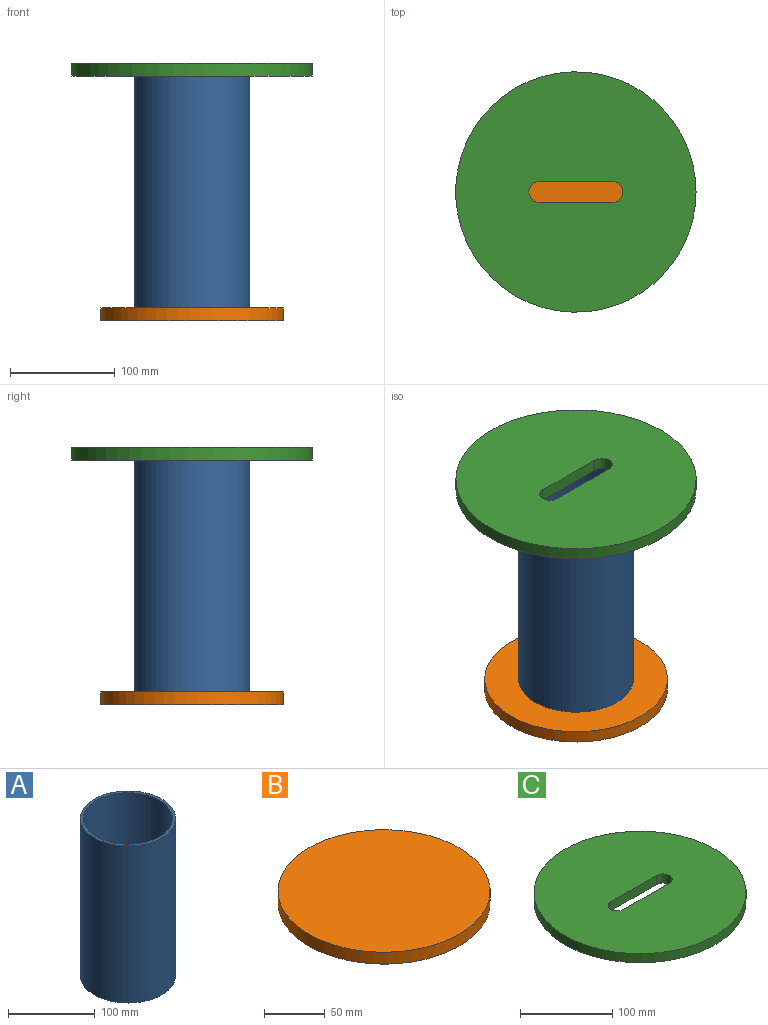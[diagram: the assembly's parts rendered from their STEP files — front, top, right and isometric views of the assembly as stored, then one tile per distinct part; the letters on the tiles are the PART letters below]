
ASSEMBLY  parts=3 mates=3
PART A: 4 faces, bbox 110x110x222 mm
  f0: cylinder r=51.5mm len=222mm, axis (0,0,-1), area 71835.7mm2, adj f2,f3
  f1: cylinder r=55mm len=222mm, axis (0,0,-1), area 76717.7mm2, adj f2,f3
  f2: plane 110x110mm, normal (0,0,1), area 1171mm2, adj f0,f1
  f3: plane 110x110mm, normal (0,0,-1), area 1171mm2, adj f0,f1
PART B: 3 faces, bbox 175x175x12 mm
  f0: cylinder r=87.5mm len=175mm, axis (0,0,-1), area 6597.3mm2, adj f1,f2
  f1: plane 175x175mm, normal (0,0,1), area 24052.8mm2, adj f0
  f2: plane 175x175mm, normal (0,0,-1), area 24052.8mm2, adj f0
PART C: 7 faces, bbox 230x230x12 mm
  f0: cylinder r=115mm len=230mm, axis (0,0,-1), area 8670.8mm2, adj f1,f2
  f1: plane 230x230mm, normal (0,0,1), area 39833.4mm2, adj f0,f3,f4,f5,f6
  f2: plane 230x230mm, normal (0,0,-1), area 39833.4mm2, adj f0,f3,f4,f5,f6
  f3: plane 70x12mm, normal (0,-1,0), area 840mm2, adj f1,f2,f4,f6
  f4: cylinder r=10mm len=20mm, axis (0,0,1), area 377mm2, adj f1,f2,f3,f5
  f5: plane 70x12mm, normal (0,1,0), area 840mm2, adj f1,f2,f4,f6
  f6: cylinder r=10mm len=20mm, axis (0,0,1), area 377mm2, adj f1,f2,f3,f5
PLACE A t=(0,0,12)mm
PLACE B at identity
PLACE C t=(0,0,234)mm
MATE cylindrical C.f0 <-> A.f1  axis (0,0,-1) through (0,0,240)mm
MATE planar A.f1 <-> B.f0  axis (0,0,-1) through (0,0,12)mm
MATE planar A.f1 <-> C.f0  axis (0,0,1) through (0,0,234)mm
